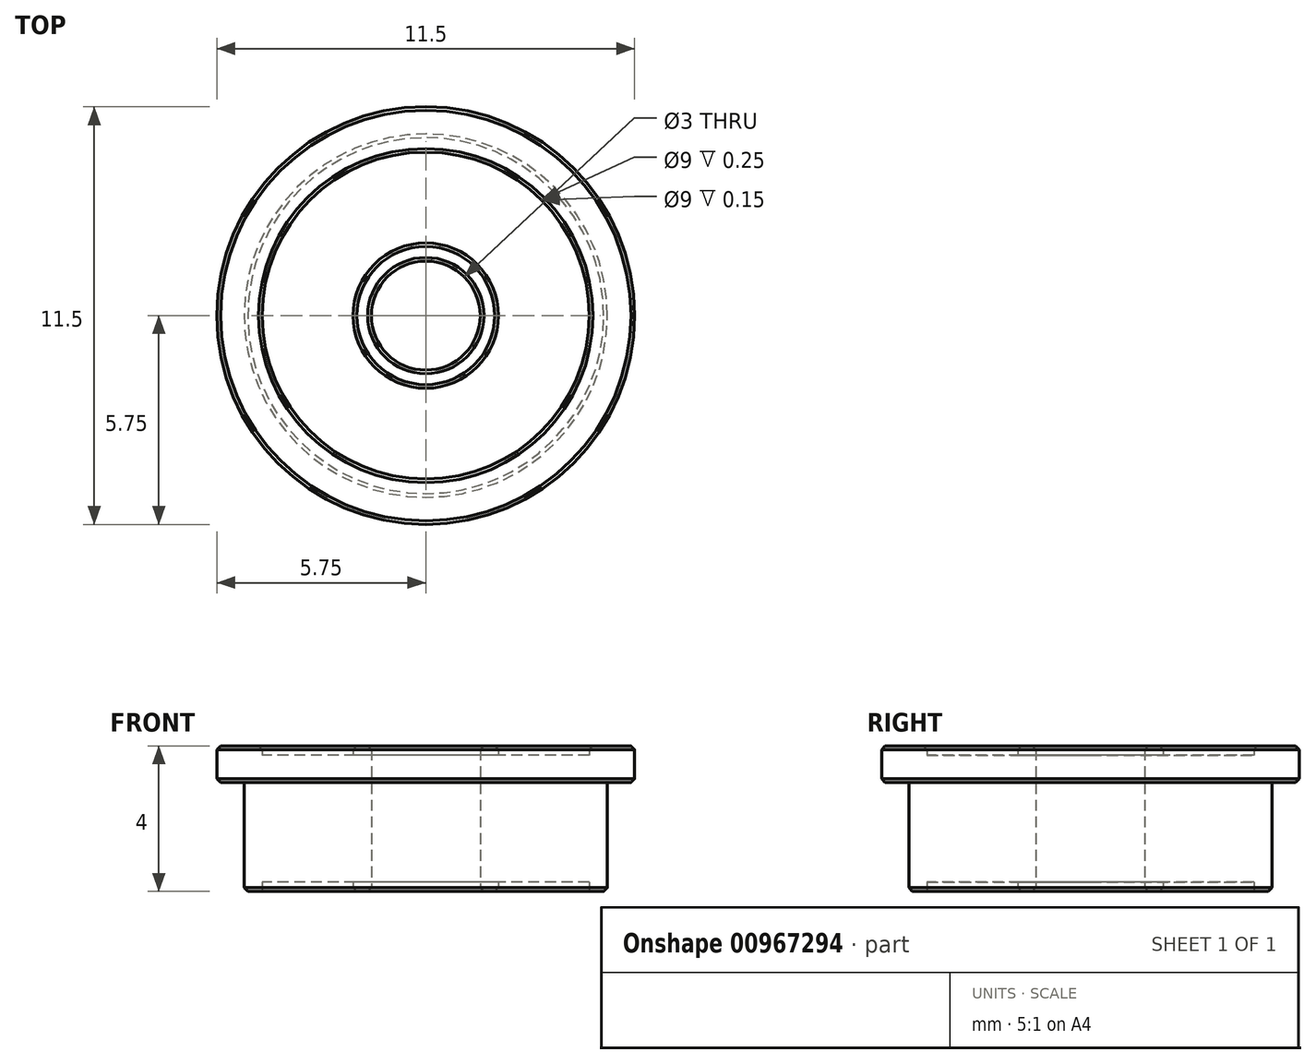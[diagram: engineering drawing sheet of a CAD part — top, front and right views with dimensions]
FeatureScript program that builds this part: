
annotation { "Feature Type Name" : "Feature", "Feature Type Description" : "" }
export const myFeature = defineFeature(function(context is Context, id is Id, definition is map)
    precondition{}
    {
        {
            var Q0;
            Q0=qCreatedBy(makeId("Top.planeOp"),FACE);
            var sketch = newSketch(context, id + "F0", { "sketchPlane" : qUnion([Q0])});
            skCircle(sketch, "E0", {"center": v(0, 0) * mm, "radius": 1.5 * mm});
            skCircle(sketch, "E1", {"center": v(0, 0) * mm, "radius": 5 * mm});
            skCircle(sketch, "E2", {"center": v(0, 0) * mm, "radius": 2 * mm});
            skCircle(sketch, "E3", {"center": v(0, 0) * mm, "radius": 4.5 * mm});
            skSolve(sketch);
        }
        {
            var Q0;
            Q0=makeQuery(id+"F0.imprint","IMPRINT",FACE,{"disambiguationData":[TD([[makeQuery(id+"F0.imprint","IMPRINT",EDGE,{"derivedFrom":sQuery(id+"F0.wireOp",EDGE,"E0")}),-1.0]])]});
            var Q1;
            Q1=makeQuery(id+"F0.imprint","IMPRINT",FACE,{"disambiguationData":[TD([[makeQuery(id+"F0.imprint","IMPRINT",EDGE,{"derivedFrom":sQuery(id+"F0.wireOp",EDGE,"E1")}),1.0]])]});
            extrude(context, id + "F1", {"entities" : qUnion([Q0, Q1]), "depth" : 0.25 * mm, "offsetDistance" : 25 * mm});
        }
        {
            var Q0;
            Q0=makeQuery(id+"F1.opExtrude","CAP_FACE",FACE,{"disambiguationData":[OSD([sQuery(id+"F0.wireOp",EDGE,"E1"),sQuery(id+"F0.wireOp",EDGE,"E3")])],"isStart":false});
            var sketch = newSketch(context, id + "F2", { "sketchPlane" : qUnion([Q0])});
            skCircle(sketch, "E4.0", {"center": v(0, 0) * mm, "radius": 2 * mm});
            skCircle(sketch, "E4.1", {"center": v(0, 0) * mm, "radius": 1.5 * mm});
            skSolve(sketch);
        }
        {
            var Q0;
            Q0=makeQuery(id+"F2.imprint","IMPRINT",FACE,{"disambiguationData":[TD([[makeQuery(id+"F2.imprint","IMPRINT",EDGE,{"derivedFrom":sQuery(id+"F2.wireOp",EDGE,"E4.0")}),-1.0]])]});
            var Q1;
            Q1=makeQuery(id+"F2.imprint","IMPRINT",FACE,{"disambiguationData":[TD([[makeQuery(id+"F2.imprint","IMPRINT",EDGE,{"derivedFrom":makeQuery(id+"F1.opExtrude","CAP_EDGE",EDGE,{"disambiguationData":[OSD([sQuery(id+"F0.wireOp",EDGE,"E1")])],"isStart":false})}),1.0]])]});
            var Q2;
            Q2=makeQuery(id+"F2.imprint","IMPRINT",FACE,{"disambiguationData":[TD([[makeQuery(id+"F2.imprint","IMPRINT",EDGE,{"derivedFrom":sQuery(id+"F2.wireOp",EDGE,"E4.0")}),1.0]])]});
            extrude(context, id + "F3", {"entities" : qUnion([Q0, Q1, Q2]), "operationType" : NewBodyOperationType.ADD, "depth" : 2.75 * mm, "offsetDistance" : 25 * mm});
        }
        {
            var Q0;
            Q0=makeQuery(id+"F3.opExtrude","CAP_FACE",FACE,{"disambiguationData":[OSD([sQuery(id+"F0.wireOp",EDGE,"E1"),sQuery(id+"F2.wireOp",EDGE,"E4.1")])],"isStart":false});
            var sketch = newSketch(context, id + "F4", { "sketchPlane" : qUnion([Q0])});
            skCircle(sketch, "E5", {"center": v(0, 0) * mm, "radius": 5.75 * mm});
            skSolve(sketch);
        }
        {
            var Q0;
            Q0=makeQuery(id+"F4.imprint","IMPRINT",FACE,{"disambiguationData":[TD([[makeQuery(id+"F4.imprint","IMPRINT",EDGE,{"derivedFrom":sQuery(id+"F4.wireOp",EDGE,"E5")}),1.0]])]});
            var Q1;
            Q1=makeQuery(id+"F4.imprint","IMPRINT",FACE,{"disambiguationData":[TD([[makeQuery(id+"F4.imprint","IMPRINT",EDGE,{"derivedFrom":makeQuery(id+"F3.opExtrude","CAP_EDGE",EDGE,{"disambiguationData":[OSD([sQuery(id+"F2.wireOp",EDGE,"E4.1")])],"isStart":false})}),-1.0]])]});
            extrude(context, id + "F5", {"entities" : qUnion([Q0, Q1]), "operationType" : NewBodyOperationType.ADD, "depth" : 0.75 * mm, "offsetDistance" : 25 * mm});
        }
        {
            var Q0;
            Q0=makeQuery(id+"F5.opExtrude","CAP_FACE",FACE,{"disambiguationData":[OSD([sQuery(id+"F2.wireOp",EDGE,"E4.1"),sQuery(id+"F4.wireOp",EDGE,"E5")])],"isStart":false});
            var sketch = newSketch(context, id + "F6", { "sketchPlane" : qUnion([Q0])});
            skCircle(sketch, "E6.0", {"center": v(0, 0) * mm, "radius": 4.5 * mm});
            skCircle(sketch, "E6.1", {"center": v(0, 0) * mm, "radius": 2 * mm});
            skSolve(sketch);
        }
        {
            var Q0;
            Q0=makeQuery(id+"F6.imprint","IMPRINT",FACE,{"disambiguationData":[TD([[makeQuery(id+"F6.imprint","IMPRINT",EDGE,{"derivedFrom":sQuery(id+"F6.wireOp",EDGE,"E6.0")}),-1.0]])]});
            var Q1;
            Q1=makeQuery(id+"F6.imprint","IMPRINT",FACE,{"disambiguationData":[TD([[makeQuery(id+"F6.imprint","IMPRINT",EDGE,{"derivedFrom":sQuery(id+"F6.wireOp",EDGE,"E6.1")}),1.0]])]});
            extrude(context, id + "F7", {"entities" : qUnion([Q0, Q1]), "operationType" : NewBodyOperationType.ADD, "depth" : 0.25 * mm, "offsetDistance" : 25 * mm});
        }
        {
            var Q0;
            Q0=makeQuery(id+"F1.opExtrude","CAP_EDGE",EDGE,{"disambiguationData":[OSD([sQuery(id+"F0.wireOp",EDGE,"E1")])],"isStart":true});
            var Q1;
            Q1=makeQuery(id+"F5.opExtrude","CAP_EDGE",EDGE,{"disambiguationData":[OSD([sQuery(id+"F4.wireOp",EDGE,"E5")])],"isStart":true});
            var Q2;
            Q2=makeQuery(id+"F7.opExtrude","CAP_EDGE",EDGE,{"disambiguationData":[OSD([sQuery(id+"F4.wireOp",EDGE,"E5")])],"isStart":false});
            var Q3;
            Q3=makeQuery(id+"F7.opExtrude","CAP_EDGE",EDGE,{"disambiguationData":[OSD([sQuery(id+"F6.wireOp",EDGE,"E6.0")])],"isStart":false});
            var Q4;
            Q4=makeQuery(id+"F1.opExtrude","CAP_EDGE",EDGE,{"disambiguationData":[OSD([sQuery(id+"F0.wireOp",EDGE,"E3")])],"isStart":false});
            var Q5;
            Q5=makeQuery(id+"F1.opExtrude","CAP_EDGE",EDGE,{"disambiguationData":[OSD([sQuery(id+"F0.wireOp",EDGE,"E2")])],"isStart":true});
            var Q6;
            Q6=makeQuery(id+"F1.opExtrude","CAP_EDGE",EDGE,{"disambiguationData":[OSD([sQuery(id+"F0.wireOp",EDGE,"E0")])],"isStart":true});
            var Q7;
            Q7=makeQuery(id+"F7.opExtrude","CAP_EDGE",EDGE,{"disambiguationData":[OSD([sQuery(id+"F6.wireOp",EDGE,"E6.1")])],"isStart":false});
            var Q8;
            Q8=makeQuery(id+"F7.opExtrude","CAP_EDGE",EDGE,{"disambiguationData":[OSD([sQuery(id+"F2.wireOp",EDGE,"E4.1")])],"isStart":false});
            chamfer(context, id + "F8", {"entities" : qUnion([Q0, Q1, Q2, Q3, Q4, Q5, Q6, Q7, Q8]), "width" : 0.1 * mm, "tangentPropagation" : true});
        }
    });
